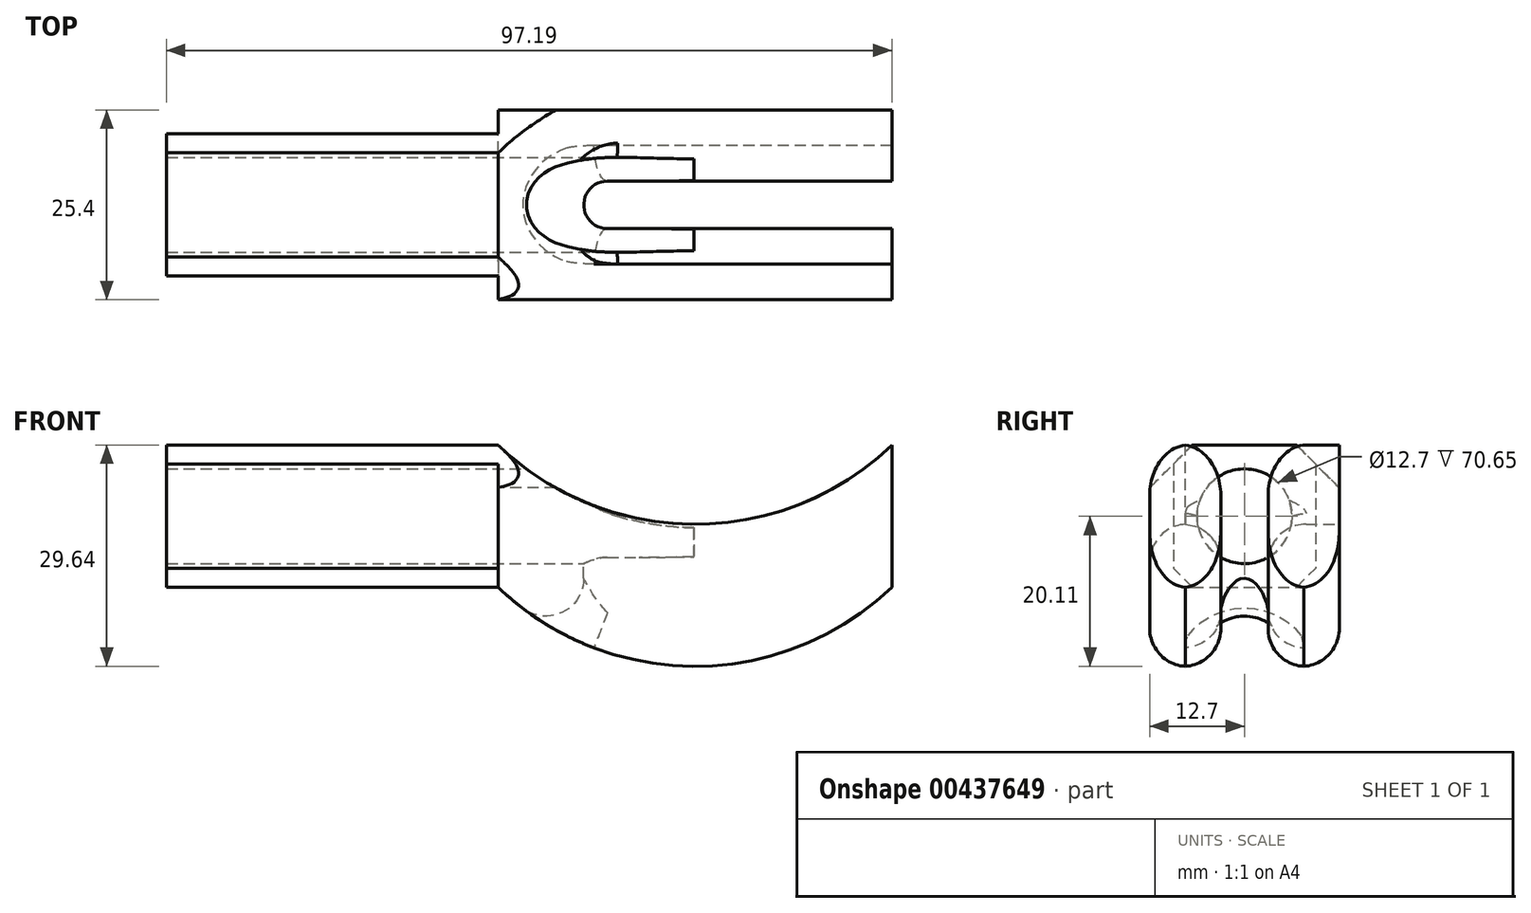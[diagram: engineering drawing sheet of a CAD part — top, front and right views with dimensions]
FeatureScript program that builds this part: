
annotation { "Feature Type Name" : "Feature", "Feature Type Description" : "" }
export const myFeature = defineFeature(function(context is Context, id is Id, definition is map)
    precondition{}
    {
        {
            var Q0;
            Q0=qCreatedBy(makeId("Front.planeOp"),FACE);
            var sketch = newSketch(context, id + "F0", { "sketchPlane" : qUnion([Q0])});
            skLineSegment(sketch, "E0.left", {"start": v(-26.2, 0) * mm, "end": v(-26.2, -19.05) * mm});
            skLineSegment(sketch, "E0.right", {"start": v(26.54, 0) * mm, "end": v(26.54, -19.05) * mm});
            skArc(sketch, "E1", {"start": v(-26.2, 0) * mm, "mid": v(0.17, -10.6) * mm, "end": v(26.54, 0) * mm});
            skArc(sketch, "E2", {"start": v(-26.2, -19.05) * mm, "mid": v(0.17, -29.65) * mm, "end": v(26.54, -19.05) * mm});
            skSolve(sketch);
        }
        {
            var Q0;
            Q0 = qSketchRegion(id + "F0", true);
            extrude(context, id + "F1", {"entities" : qUnion([Q0]), "depth" : 25.4 * mm, "offsetDistance" : 25.4 * mm});
        }
        {
            var Q0;
            Q0=qCreatedBy(makeId("Top.planeOp"),FACE);
            var sketch = newSketch(context, id + "F2", { "sketchPlane" : qUnion([Q0])});
            skLineSegment(sketch, "E3", {"start": v(26.54, 0) * mm, "end": v(26.54, -9.53) * mm});
            skLineSegment(sketch, "E4", {"start": v(26.54, -9.53) * mm, "end": v(-11.56, -9.53) * mm});
            skLineSegment(sketch, "E5", {"start": v(-11.56, -15.88) * mm, "end": v(26.54, -15.88) * mm});
            skArc(sketch, "E6", {"start": v(-11.56, -9.53) * mm, "mid": v(-14.74, -12.7) * mm, "end": v(-11.56, -15.88) * mm});
            skLineSegment(sketch, "E7", {"start": v(26.54, -15.88) * mm, "end": v(26.54, -9.53) * mm});
            skLineSegment(sketch, "E8", {"start": v(26.54, 0) * mm, "end": v(26.8, 0) * mm});
            skSolve(sketch);
        }
        {
            var Q0;
            Q0 = qSketchRegion(id + "F2", true);
            extrude(context, id + "F3", {"entities" : qUnion([Q0]), "operationType" : NewBodyOperationType.REMOVE, "endBound" : BoundingType.THROUGH_ALL, "oppositeDirection" : true, "depth" : 25.4 * mm});
        }
        {
            var Q0;
            Q0=makeQuery(id+"F1.opExtrude","SWEPT_FACE",FACE,{"disambiguationData":[OSD([sQuery(id+"F0.wireOp",EDGE,"E0.left")])]});
            var sketch = newSketch(context, id + "F4", { "sketchPlane" : qUnion([Q0])});
            skLineSegment(sketch, "E9.bottom", {"start": v(3.18, 0) * mm, "end": v(22.23, 0) * mm});
            skLineSegment(sketch, "E9.top", {"start": v(3.18, -19.05) * mm, "end": v(22.23, -19.05) * mm});
            skLineSegment(sketch, "E9.left", {"start": v(3.18, 0) * mm, "end": v(3.18, -19.05) * mm});
            skLineSegment(sketch, "E9.right", {"start": v(22.23, 0) * mm, "end": v(22.23, -19.05) * mm});
            skSolve(sketch);
        }
        {
            var Q0;
            Q0 = qSketchRegion(id + "F4", true);
            extrude(context, id + "F5", {"entities" : qUnion([Q0]), "operationType" : NewBodyOperationType.ADD, "depth" : 44.45 * mm});
        }
        {
            var Q0;
            Q0=makeQuery(id+"F5.opExtrude","SWEPT_EDGE",EDGE,{"disambiguationData":[OSD([sQuery(id+"F0.wireOp",EDGE,"E1"),sQuery(id+"F0.wireOp",EDGE,"E0.left"),sQuery(id+"F4.wireOp",EDGE,"E9.bottom"),sQuery(id+"F4.wireOp",EDGE,"E9.right")])]});
            var Q1;
            Q1=makeQuery(id+"F5.opExtrude","SWEPT_EDGE",EDGE,{"disambiguationData":[OSD([sQuery(id+"F0.wireOp",EDGE,"E0.left"),sQuery(id+"F0.wireOp",EDGE,"E2"),sQuery(id+"F4.wireOp",EDGE,"E9.top"),sQuery(id+"F4.wireOp",EDGE,"E9.left")])]});
            var Q2;
            Q2=makeQuery(id+"F5.opExtrude","SWEPT_EDGE",EDGE,{"disambiguationData":[OSD([sQuery(id+"F0.wireOp",EDGE,"E0.left"),sQuery(id+"F0.wireOp",EDGE,"E2"),sQuery(id+"F4.wireOp",EDGE,"E9.top"),sQuery(id+"F4.wireOp",EDGE,"E9.right")])]});
            var Q3;
            Q3=makeQuery(id+"F5.opExtrude","SWEPT_EDGE",EDGE,{"disambiguationData":[OSD([sQuery(id+"F0.wireOp",EDGE,"E1"),sQuery(id+"F0.wireOp",EDGE,"E0.left"),sQuery(id+"F4.wireOp",EDGE,"E9.bottom"),sQuery(id+"F4.wireOp",EDGE,"E9.left")])]});
            chamfer(context, id + "F6", {"entities" : qUnion([Q0, Q1, Q2, Q3]), "width" : 2.54 * mm, "tangentPropagation" : true});
        }
        {
            var Q0;
            Q0=makeQuery(id+"F1.opExtrude","CAP_EDGE",EDGE,{"disambiguationData":[OSD([sQuery(id+"F0.wireOp",EDGE,"E1")])],"isStart":false});
            var Q1;
            Q1=makeQuery(id+"F3.boolean.opBoolean","INTERSECT",EDGE,{"derivedFrom":[makeQuery(id+"F1.opExtrude","SWEPT_FACE",FACE,{"disambiguationData":[OSD([sQuery(id+"F0.wireOp",EDGE,"E1")])]}),makeQuery(id+"F3.opExtrude","SWEPT_FACE",FACE,{"disambiguationData":[OSD([sQuery(id+"F2.wireOp",EDGE,"E5")])]})]});
            var Q2;
            Q2=makeQuery(id+"F3.boolean.opBoolean","INTERSECT",EDGE,{"derivedFrom":[makeQuery(id+"F1.opExtrude","SWEPT_FACE",FACE,{"disambiguationData":[OSD([sQuery(id+"F0.wireOp",EDGE,"E1")])]}),makeQuery(id+"F3.opExtrude","SWEPT_FACE",FACE,{"disambiguationData":[OSD([sQuery(id+"F2.wireOp",EDGE,"E4")])]})]});
            var Q3;
            Q3=makeQuery(id+"F1.opExtrude","CAP_EDGE",EDGE,{"disambiguationData":[OSD([sQuery(id+"F0.wireOp",EDGE,"E2")])],"isStart":false});
            var Q4;
            Q4=makeQuery(id+"F3.boolean.opBoolean","INTERSECT",EDGE,{"derivedFrom":[makeQuery(id+"F1.opExtrude","SWEPT_FACE",FACE,{"disambiguationData":[OSD([sQuery(id+"F0.wireOp",EDGE,"E2")])]}),makeQuery(id+"F3.opExtrude","SWEPT_FACE",FACE,{"disambiguationData":[OSD([sQuery(id+"F2.wireOp",EDGE,"E4")])]})]});
            var Q5;
            Q5=makeQuery(id+"F3.boolean.opBoolean","INTERSECT",EDGE,{"derivedFrom":[makeQuery(id+"F1.opExtrude","SWEPT_FACE",FACE,{"disambiguationData":[OSD([sQuery(id+"F0.wireOp",EDGE,"E2")])]}),makeQuery(id+"F3.opExtrude","SWEPT_FACE",FACE,{"disambiguationData":[OSD([sQuery(id+"F2.wireOp",EDGE,"E5")])]})]});
            var Q6;
            Q6=makeQuery(id+"F1.opExtrude","CAP_EDGE",EDGE,{"disambiguationData":[OSD([sQuery(id+"F0.wireOp",EDGE,"E2")])],"isStart":true});
            fillet(context, id + "F7", {"entities" : qUnion([Q0, Q1, Q2, Q3, Q4, Q5, Q6]), "radius" : 5.08 * mm, "tangentPropagation" : true, "allowEdgeOverflow" : false});
        }
        {
            var Q0;
            Q0=qCreatedBy(makeId("Right.planeOp"),FACE);
            var sketch = newSketch(context, id + "F8", { "sketchPlane" : qUnion([Q0])});
            skPoint(sketch, "E10", {"position": v(-12.7, -9.53) * mm});
            skSolve(sketch);
        }
        {
            var Q0;
            Q0=sQuery(id+"F8.wireOp",VERTEX,"E10");
            var Q1;
            Q1=makeQuery(id+"F1.opExtrude","SWEPT_BODY",BODY,{"disambiguationData":[OSD([sQuery(id+"F0.wireOp",EDGE,"E0.right"),sQuery(id+"F0.wireOp",EDGE,"E1"),sQuery(id+"F0.wireOp",EDGE,"E0.left"),sQuery(id+"F0.wireOp",EDGE,"E2")])]});
            hole(context, id + "F9", {"style" : HoleStyle.SIMPLE, "endStyle" : HoleEndStyle.THROUGH, "holeDiameter" : 12.7 * mm, "isTappedThrough" : true, "tappedDepth" : 12.7 * mm, "tapClearance" : 3, "locations" : qUnion([Q0]), "scope" : qUnion([Q1])});
        }
    });
